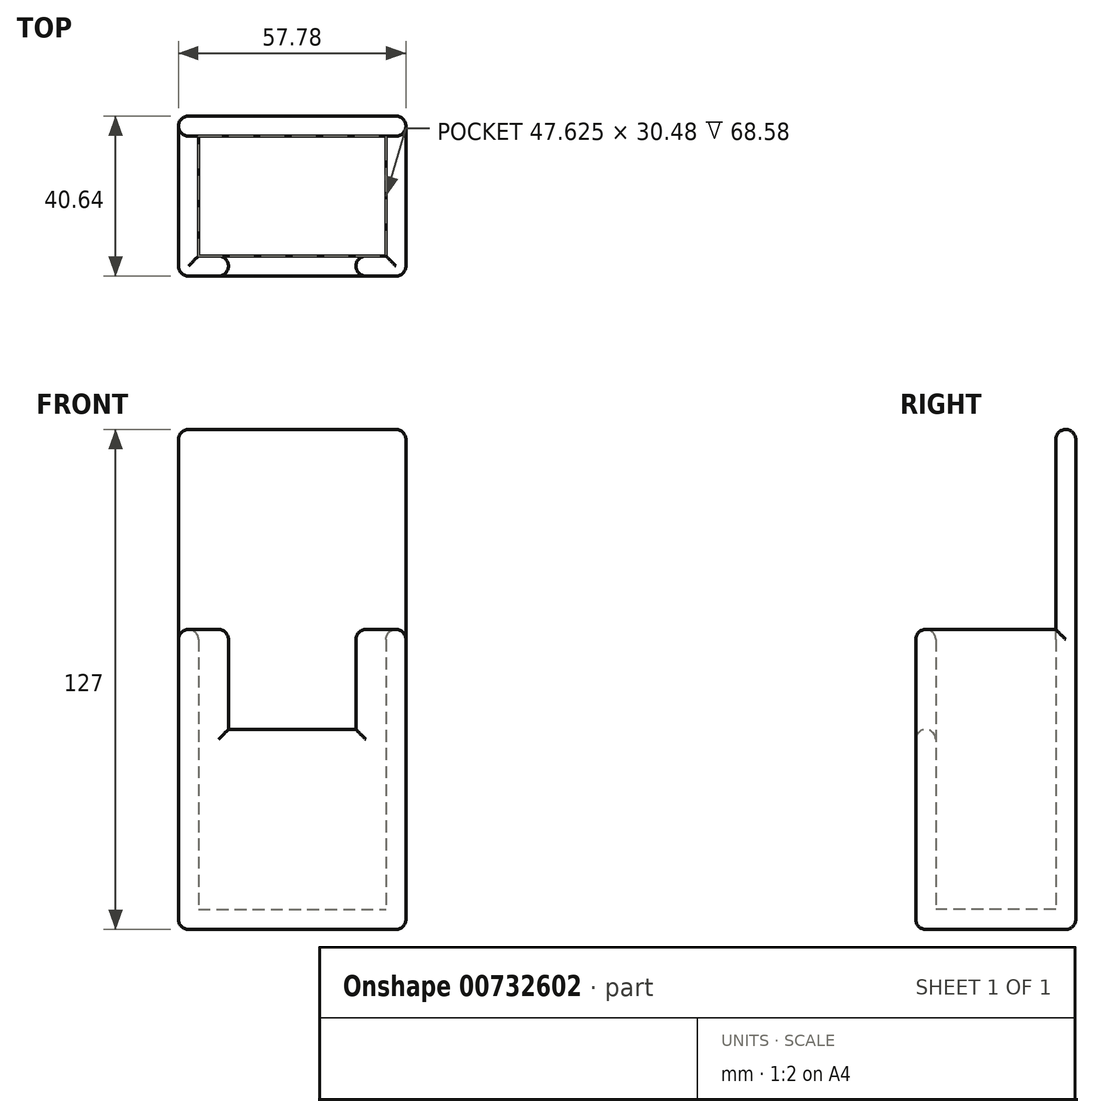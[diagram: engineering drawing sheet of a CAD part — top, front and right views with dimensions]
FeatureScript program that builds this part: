
annotation { "Feature Type Name" : "Feature", "Feature Type Description" : "" }
export const myFeature = defineFeature(function(context is Context, id is Id, definition is map)
    precondition{}
    {
        {
            var Q0;
            Q0=qCreatedBy(makeId("Top.planeOp"),FACE);
            var sketch = newSketch(context, id + "F0", { "sketchPlane" : qUnion([Q0])});
            skLineSegment(sketch, "E0.bottom", {"start": v(-28.9, 20.32) * mm, "end": v(28.9, 20.32) * mm});
            skLineSegment(sketch, "E0.top", {"start": v(-28.9, -20.32) * mm, "end": v(28.9, -20.32) * mm});
            skLineSegment(sketch, "E0.left", {"start": v(-28.9, 20.32) * mm, "end": v(-28.9, -20.32) * mm});
            skLineSegment(sketch, "E0.right", {"start": v(28.9, 20.32) * mm, "end": v(28.9, -20.32) * mm});
            skPoint(sketch, "E0.middle", {"position": v(0, 0) * mm});
            skLineSegment(sketch, "E1.0", {"start": v(-23.81, 15.24) * mm, "end": v(23.81, 15.24) * mm});
            skLineSegment(sketch, "E1.1", {"start": v(-23.81, 15.24) * mm, "end": v(-23.81, -15.24) * mm});
            skLineSegment(sketch, "E1.2", {"start": v(-23.81, -15.24) * mm, "end": v(23.81, -15.24) * mm});
            skLineSegment(sketch, "E1.3", {"start": v(23.81, 15.24) * mm, "end": v(23.81, -15.24) * mm});
            skLineSegment(sketch, "E2", {"start": v(-16.2, -15.24) * mm, "end": v(-16.2, -20.32) * mm});
            skLineSegment(sketch, "E3", {"start": v(16.2, -15.24) * mm, "end": v(16.2, -20.32) * mm});
            skLineSegment(sketch, "E4", {"start": v(-23.81, 15.24) * mm, "end": v(-28.9, 15.24) * mm});
            skLineSegment(sketch, "E5", {"start": v(23.81, 15.24) * mm, "end": v(28.9, 15.24) * mm});
            skSolve(sketch);
        }
        {
            var Q0;
            Q0=makeQuery(id+"F0.imprint","IMPRINT",FACE,{"disambiguationData":[TD([[makeQuery(id+"F0.imprint","IMPRINT",EDGE,{"derivedFrom":sQuery(id+"F0.wireOp",EDGE,"E1.0")}),-1.0]])]});
            extrude(context, id + "F1", {"entities" : qUnion([Q0]), "depth" : 5.08 * mm, "offsetDistance" : 25.4 * mm});
        }
        {
            var Q0;
            {var subQ0=sQuery(id+"F0.wireOp",EDGE,"E2");Q0=makeQuery(id+"F0.imprint","IMPRINT",FACE,{"disambiguationData":[TD([[makeQuery(id+"F0.imprint","IMPRINT",EDGE,{"derivedFrom":subQ0}),1.0]])]});}
            extrude(context, id + "F2", {"entities" : qUnion([Q0]), "operationType" : NewBodyOperationType.ADD, "depth" : 50.8 * mm, "offsetDistance" : 25.4 * mm});
        }
        {
            var Q0;
            {var subQ0=sQuery(id+"F0.wireOp",EDGE,"E1.1");Q0=makeQuery(id+"F0.imprint","IMPRINT",FACE,{"disambiguationData":[TD([[makeQuery(id+"F0.imprint","IMPRINT",EDGE,{"derivedFrom":subQ0}),-1.0]])]});}
            var Q1;
            {var subQ0=sQuery(id+"F0.wireOp",EDGE,"E1.3");Q1=makeQuery(id+"F0.imprint","IMPRINT",FACE,{"disambiguationData":[TD([[makeQuery(id+"F0.imprint","IMPRINT",EDGE,{"derivedFrom":subQ0}),1.0]])]});}
            extrude(context, id + "F3", {"entities" : qUnion([Q0, Q1]), "operationType" : NewBodyOperationType.ADD, "depth" : 76.2 * mm, "offsetDistance" : 25.4 * mm});
        }
        {
            var Q0;
            {var subQ1=sQuery(id+"F0.wireOp",EDGE,"E0.bottom");Q0=makeQuery(id+"F0.imprint","IMPRINT",FACE,{"disambiguationData":[TD([[makeQuery(id+"F0.imprint","IMPRINT",EDGE,{"derivedFrom":subQ1}),-1.0]])]});}
            extrude(context, id + "F4", {"entities" : qUnion([Q0]), "operationType" : NewBodyOperationType.ADD, "depth" : 127 * mm, "offsetDistance" : 25.4 * mm});
        }
        {
            var Q0;
            Q0=makeQuery(id+"F3.opExtrude","SWEPT_EDGE",EDGE,{"disambiguationData":[OSD([sQuery(id+"F0.wireOp",EDGE,"E0.top"),sQuery(id+"F0.wireOp",EDGE,"E0.right")])]});
            var Q1;
            {var subQ0=sQuery(id+"F0.wireOp",EDGE,"E0.top");Q1=makeQuery(id+"F3.opExtrude","CAP_EDGE",EDGE,{"disambiguationData":[OSD([subQ0]),TDD([makeQuery(id+"F0.imprint","IMPRINT",EDGE,{"disambiguationData":[TD([[makeQuery(id+"F0.imprint","INTERSECT",VERTEX,{"derivedFrom":[subQ0,sQuery(id+"F0.wireOp",EDGE,"E0.right")]}),1.0]])],"derivedFrom":subQ0})])],"isStart":false});}
            var Q2;
            Q2=makeQuery(id+"F3.opExtrude","SWEPT_EDGE",EDGE,{"disambiguationData":[OSD([sQuery(id+"F0.wireOp",EDGE,"E0.top"),sQuery(id+"F0.wireOp",EDGE,"E3")])]});
            var Q3;
            Q3=makeQuery(id+"F2.opExtrude","CAP_EDGE",EDGE,{"disambiguationData":[OSD([sQuery(id+"F0.wireOp",EDGE,"E0.top")])],"isStart":false});
            var Q4;
            Q4=makeQuery(id+"F3.opExtrude","SWEPT_EDGE",EDGE,{"disambiguationData":[OSD([sQuery(id+"F0.wireOp",EDGE,"E0.top"),sQuery(id+"F0.wireOp",EDGE,"E2")])]});
            var Q5;
            {var subQ0=sQuery(id+"F0.wireOp",EDGE,"E0.top");Q5=makeQuery(id+"F3.opExtrude","CAP_EDGE",EDGE,{"disambiguationData":[OSD([subQ0]),TDD([makeQuery(id+"F0.imprint","IMPRINT",EDGE,{"disambiguationData":[TD([[makeQuery(id+"F0.imprint","INTERSECT",VERTEX,{"derivedFrom":[subQ0,sQuery(id+"F0.wireOp",EDGE,"E0.left")]}),-1.0]])],"derivedFrom":subQ0})])],"isStart":false});}
            var Q6;
            {var subQ0=sQuery(id+"F0.wireOp",EDGE,"E0.top");Q6=makeQuery(id+"F3.boolean.opBoolean","MERGE",FACE,{"derivedFrom":[makeQuery(id+"F2.opExtrude","SWEPT_FACE",FACE,{"disambiguationData":[OSD([subQ0])]}),makeQuery(id+"F3.opExtrude","SWEPT_FACE",FACE,{"disambiguationData":[OSD([subQ0]),TDD([makeQuery(id+"F0.imprint","IMPRINT",EDGE,{"disambiguationData":[TD([[makeQuery(id+"F0.imprint","INTERSECT",VERTEX,{"derivedFrom":[subQ0,sQuery(id+"F0.wireOp",EDGE,"E0.left")]}),-1.0]])],"derivedFrom":subQ0})])]}),makeQuery(id+"F3.opExtrude","SWEPT_FACE",FACE,{"disambiguationData":[OSD([subQ0]),TDD([makeQuery(id+"F0.imprint","IMPRINT",EDGE,{"disambiguationData":[TD([[makeQuery(id+"F0.imprint","INTERSECT",VERTEX,{"derivedFrom":[subQ0,sQuery(id+"F0.wireOp",EDGE,"E0.right")]}),1.0]])],"derivedFrom":subQ0})])]})]});}
            var Q7;
            Q7=makeQuery(id+"F3.opExtrude","SWEPT_EDGE",EDGE,{"disambiguationData":[OSD([sQuery(id+"F0.wireOp",EDGE,"E1.2"),sQuery(id+"F0.wireOp",EDGE,"E2")])]});
            var Q8;
            Q8=makeQuery(id+"F2.opExtrude","CAP_EDGE",EDGE,{"disambiguationData":[OSD([sQuery(id+"F0.wireOp",EDGE,"E1.2")])],"isStart":false});
            var Q9;
            {var subQ0=sQuery(id+"F0.wireOp",EDGE,"E1.2");Q9=makeQuery(id+"F3.opExtrude","CAP_EDGE",EDGE,{"disambiguationData":[OSD([subQ0]),TDD([makeQuery(id+"F0.imprint","IMPRINT",EDGE,{"disambiguationData":[TD([[makeQuery(id+"F0.imprint","INTERSECT",VERTEX,{"derivedFrom":[sQuery(id+"F0.wireOp",EDGE,"E1.1"),subQ0]}),-1.0]])],"derivedFrom":subQ0})])],"isStart":false});}
            var Q10;
            {var subQ0=sQuery(id+"F0.wireOp",EDGE,"E1.2");Q10=makeQuery(id+"F3.opExtrude","CAP_EDGE",EDGE,{"disambiguationData":[OSD([subQ0]),TDD([makeQuery(id+"F0.imprint","IMPRINT",EDGE,{"disambiguationData":[TD([[makeQuery(id+"F0.imprint","INTERSECT",VERTEX,{"derivedFrom":[subQ0,sQuery(id+"F0.wireOp",EDGE,"E1.3")]}),1.0]])],"derivedFrom":subQ0})])],"isStart":false});}
            var Q11;
            Q11=makeQuery(id+"F3.opExtrude","SWEPT_EDGE",EDGE,{"disambiguationData":[OSD([sQuery(id+"F0.wireOp",EDGE,"E1.2"),sQuery(id+"F0.wireOp",EDGE,"E3")])]});
            var Q12;
            Q12=makeQuery(id+"F3.opExtrude","CAP_EDGE",EDGE,{"disambiguationData":[OSD([sQuery(id+"F0.wireOp",EDGE,"E3")])],"isStart":false});
            var Q13;
            Q13=makeQuery(id+"F3.opExtrude","CAP_EDGE",EDGE,{"disambiguationData":[OSD([sQuery(id+"F0.wireOp",EDGE,"E2")])],"isStart":false});
            var Q14;
            Q14=makeQuery(id+"F3.opExtrude","CAP_EDGE",EDGE,{"disambiguationData":[OSD([sQuery(id+"F0.wireOp",EDGE,"E1.3")])],"isStart":false});
            var Q15;
            Q15=makeQuery(id+"F3.opExtrude","CAP_EDGE",EDGE,{"disambiguationData":[OSD([sQuery(id+"F0.wireOp",EDGE,"E1.1")])],"isStart":false});
            var Q16;
            Q16=makeQuery(id+"F3.opExtrude","CAP_EDGE",EDGE,{"disambiguationData":[OSD([sQuery(id+"F0.wireOp",EDGE,"E0.right")])],"isStart":false});
            var Q17;
            Q17=makeQuery(id+"F4.opExtrude","SWEPT_EDGE",EDGE,{"disambiguationData":[OSD([sQuery(id+"F0.wireOp",EDGE,"E0.right"),sQuery(id+"F0.wireOp",EDGE,"E5")])]});
            var Q18;
            Q18=makeQuery(id+"F4.opExtrude","CAP_EDGE",EDGE,{"disambiguationData":[OSD([sQuery(id+"F0.wireOp",EDGE,"E0.right")])],"isStart":false});
            var Q19;
            Q19=makeQuery(id+"F4.opExtrude","SWEPT_EDGE",EDGE,{"disambiguationData":[OSD([sQuery(id+"F0.wireOp",EDGE,"E0.bottom"),sQuery(id+"F0.wireOp",EDGE,"E0.right")])]});
            var Q20;
            {var subQ0=sQuery(id+"F0.wireOp",EDGE,"E0.right");Q20=makeQuery(id+"F4.boolean.opBoolean","MERGE",EDGE,{"derivedFrom":[makeQuery(id+"F3.opExtrude","CAP_EDGE",EDGE,{"disambiguationData":[OSD([subQ0])],"isStart":true}),makeQuery(id+"F4.opExtrude","CAP_EDGE",EDGE,{"disambiguationData":[OSD([subQ0])],"isStart":true})]});}
            var Q21;
            Q21=makeQuery(id+"F4.opExtrude","CAP_EDGE",EDGE,{"disambiguationData":[OSD([sQuery(id+"F0.wireOp",EDGE,"E1.0"),sQuery(id+"F0.wireOp",EDGE,"E4"),sQuery(id+"F0.wireOp",EDGE,"E5")])],"isStart":false});
            var Q22;
            Q22=makeQuery(id+"F4.opExtrude","SWEPT_EDGE",EDGE,{"disambiguationData":[OSD([sQuery(id+"F0.wireOp",EDGE,"E0.left"),sQuery(id+"F0.wireOp",EDGE,"E4")])]});
            var Q23;
            Q23=makeQuery(id+"F4.opExtrude","CAP_EDGE",EDGE,{"disambiguationData":[OSD([sQuery(id+"F0.wireOp",EDGE,"E0.bottom")])],"isStart":false});
            var Q24;
            Q24=makeQuery(id+"F4.opExtrude","SWEPT_EDGE",EDGE,{"disambiguationData":[OSD([sQuery(id+"F0.wireOp",EDGE,"E0.bottom"),sQuery(id+"F0.wireOp",EDGE,"E0.left")])]});
            var Q25;
            Q25=makeQuery(id+"F3.opExtrude","CAP_EDGE",EDGE,{"disambiguationData":[OSD([sQuery(id+"F0.wireOp",EDGE,"E0.left")])],"isStart":false});
            var Q26;
            {var subQ0=sQuery(id+"F0.wireOp",EDGE,"E0.left");Q26=makeQuery(id+"F4.boolean.opBoolean","MERGE",EDGE,{"derivedFrom":[makeQuery(id+"F3.opExtrude","CAP_EDGE",EDGE,{"disambiguationData":[OSD([subQ0])],"isStart":true}),makeQuery(id+"F4.opExtrude","CAP_EDGE",EDGE,{"disambiguationData":[OSD([subQ0])],"isStart":true})]});}
            var Q27;
            Q27=makeQuery(id+"F4.opExtrude","CAP_EDGE",EDGE,{"disambiguationData":[OSD([sQuery(id+"F0.wireOp",EDGE,"E0.bottom")])],"isStart":true});
            var Q28;
            Q28=makeQuery(id+"F4.opExtrude","CAP_EDGE",EDGE,{"disambiguationData":[OSD([sQuery(id+"F0.wireOp",EDGE,"E0.left")])],"isStart":false});
            fillet(context, id + "F5", {"entities" : qUnion([Q0, Q1, Q2, Q3, Q4, Q5, Q6, Q7, Q8, Q9, Q10, Q11, Q12, Q13, Q14, Q15, Q16, Q17, Q18, Q19, Q20, Q21, Q22, Q23, Q24, Q25, Q26, Q27, Q28]), "radius" : 2.54 * mm, "tangentPropagation" : true, "allowEdgeOverflow" : false});
        }
    });
